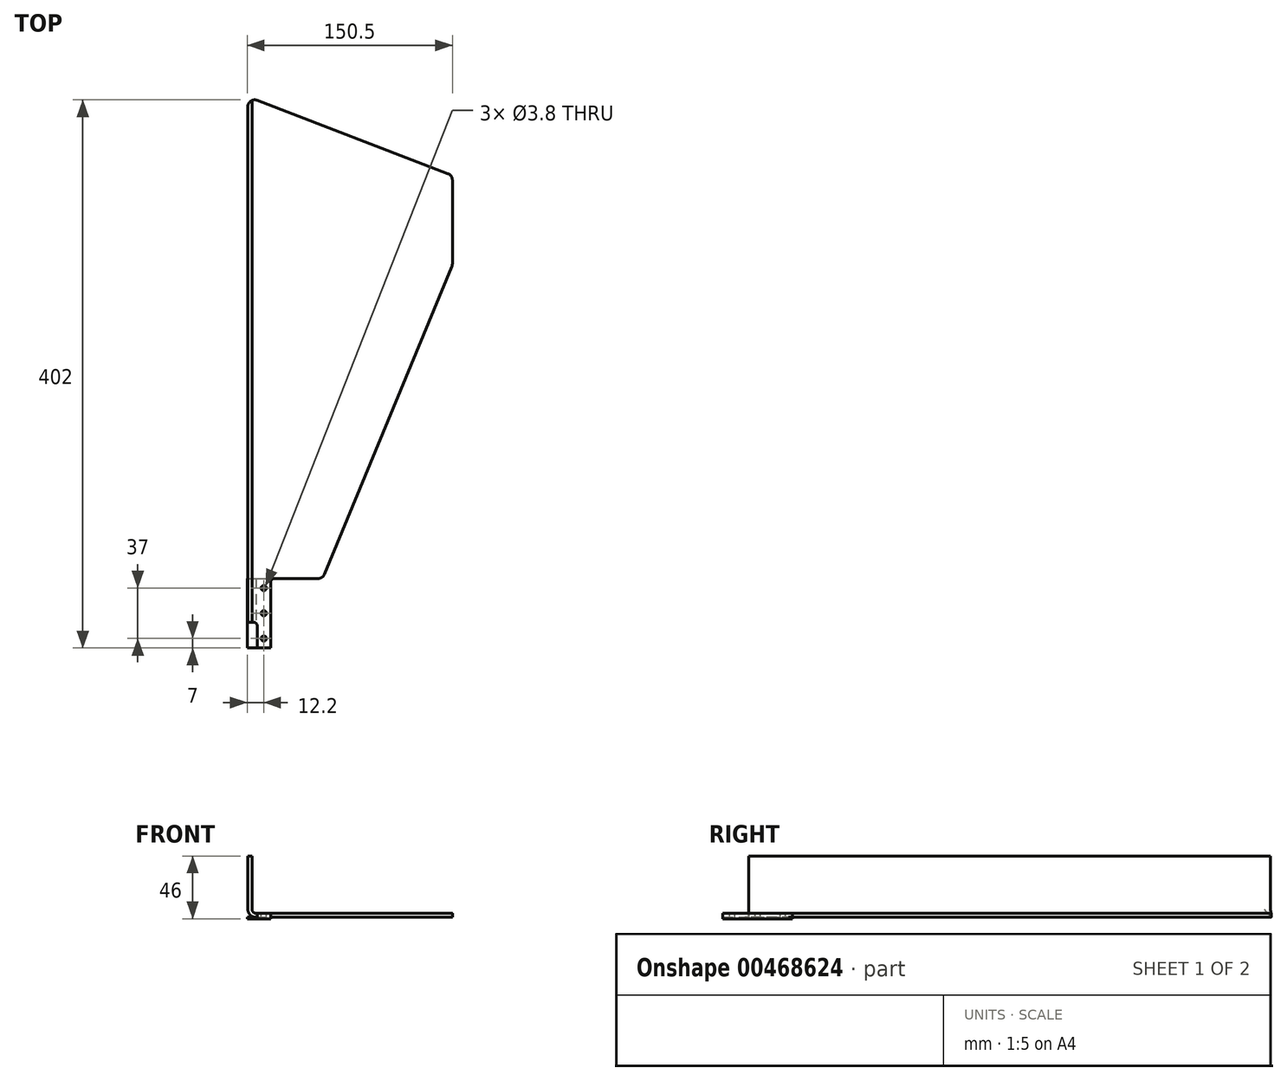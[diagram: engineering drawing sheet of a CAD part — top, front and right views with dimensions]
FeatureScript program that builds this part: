
annotation { "Feature Type Name" : "Feature", "Feature Type Description" : "" }
export const myFeature = defineFeature(function(context is Context, id is Id, definition is map)
    precondition{}
    {
        {
            var Q0;
            Q0=qCreatedBy(makeId("Front.planeOp"),FACE);
            var sketch = newSketch(context, id + "F0", { "sketchPlane" : qUnion([Q0]) });
            skLineSegment(sketch, "E0", {"start": v(-20, 42) * mm, "end": v(-20, 3) * mm});
            skLineSegment(sketch, "E1", {"start": v(-17, 0) * mm, "end": v(127, 0) * mm});
            skPoint(sketch, "E2", {"position": v(0, 0) * mm});
            skPoint(sketch, "E3.visualSharp", {"position": v(-20, 0) * mm});
            skArc(sketch, "E3.filletArc", {"start": v(-20, 3) * mm, "mid": v(-19.12, 0.88) * mm, "end": v(-17, 0) * mm});
            skLineSegment(sketch, "E4", {"start": v(-20, 42) * mm, "end": v(-23, 42) * mm});
            skLineSegment(sketch, "E5", {"start": v(-23, 42) * mm, "end": v(-23, 3) * mm});
            skLineSegment(sketch, "E6", {"start": v(-17, -3) * mm, "end": v(127, -3) * mm});
            skPoint(sketch, "E7.visualSharp", {"position": v(-23, -3) * mm});
            skArc(sketch, "E7.filletArc", {"start": v(-23, 3) * mm, "mid": v(-21.24, -1.24) * mm, "end": v(-17, -3) * mm});
            skLineSegment(sketch, "E8", {"start": v(127, 0) * mm, "end": v(127, -3) * mm});
            skSolve(sketch);
        }
        {
            var Q0;
            Q0=qSketchRegion(id+"F0",true);
            extrude(context, id + "F1", {"entities" : qUnion([Q0]), "oppositeDirection" : true, "depth" : 500 * mm});
        }
        {
            var Q0;
            Q0=qCreatedBy(makeId("Top.planeOp"),FACE);
            var sketch = newSketch(context, id + "F2", { "sketchPlane" : qUnion([Q0]) });
            skLineSegment(sketch, "E9.bottom", {"start": v(-56.37, 525.22) * mm, "end": v(165.37, 525.22) * mm});
            skLineSegment(sketch, "E9.top", {"start": v(-56.37, -13.1) * mm, "end": v(165.37, -13.1) * mm});
            skLineSegment(sketch, "E9.left", {"start": v(-56.37, 525.22) * mm, "end": v(-56.37, -13.1) * mm});
            skLineSegment(sketch, "E9.right", {"start": v(165.37, 525.22) * mm, "end": v(165.37, -13.1) * mm});
            skLineSegment(sketch, "E10.bottom", {"start": v(455.61, 344.43) * mm, "end": v(485.6, 345.09) * mm});
            skLineSegment(sketch, "E10.top", {"start": v(456.73, 293.44) * mm, "end": v(486.72, 294.1) * mm});
            skLineSegment(sketch, "E10.left", {"start": v(455.61, 344.43) * mm, "end": v(456.73, 293.44) * mm});
            skLineSegment(sketch, "E10.right", {"start": v(485.6, 345.09) * mm, "end": v(486.72, 294.1) * mm});
            skCircle(sketch, "E11", {"center": v(481.57, 300.99) * mm, "radius": 1.9 * mm});
            skCircle(sketch, "E12", {"center": v(480.76, 337.98) * mm, "radius": 1.9 * mm});
            skCircle(sketch, "E13", {"center": v(460.77, 337.54) * mm, "radius": 1.9 * mm});
            skCircle(sketch, "E14", {"center": v(461.57, 300.55) * mm, "radius": 1.9 * mm});
            skPoint(sketch, "E15", {"position": v(456.17, 318.94) * mm});
            skLineSegment(sketch, "E16.left", {"start": v(468.41, 344.71) * mm, "end": v(469.52, 293.72) * mm});
            skLineSegment(sketch, "E16.right", {"start": v(472.81, 344.8) * mm, "end": v(473.92, 293.82) * mm});
            skLineSegment(sketch, "E17.0", {"start": v(461.57, 300.55) * mm, "end": v(481.57, 300.99) * mm, "construction": true});
            skLineSegment(sketch, "E18.0", {"start": v(460.77, 337.54) * mm, "end": v(480.76, 337.98) * mm, "construction": true});
            skLineSegment(sketch, "E19.0", {"start": v(461.57, 300.55) * mm, "end": v(460.77, 337.54) * mm, "construction": true});
            skLineSegment(sketch, "E20.0", {"start": v(481.57, 300.99) * mm, "end": v(480.76, 337.98) * mm, "construction": true});
            skPoint(sketch, "E21", {"position": v(470.61, 344.76) * mm});
            skCircle(sketch, "E22", {"center": v(461.17, 319.05) * mm, "radius": 1.9 * mm});
            skCircle(sketch, "E23", {"center": v(481.16, 319.48) * mm, "radius": 1.9 * mm});
            skLineSegment(sketch, "E24", {"start": v(486.72, 294.1) * mm, "end": v(474.92, 293.84) * mm});
            skLineSegment(sketch, "E25", {"start": v(467.41, 344.69) * mm, "end": v(455.61, 344.43) * mm});
            skLineSegment(sketch, "E26.1.3", {"start": v(456.01, 326.28) * mm, "end": v(455.61, 344.43) * mm});
            skPoint(sketch, "E27", {"position": v(510.48, 432.74) * mm});
            skPoint(sketch, "E28.visualSharp", {"position": v(485.6, 345.09) * mm});
            skLineSegment(sketch, "E29", {"start": v(33.19, 54.09) * mm, "end": v(126.62, 279.65) * mm});
            skLineSegment(sketch, "E30", {"start": v(-23, 19) * mm, "end": v(-23, 397) * mm});
            skLineSegment(sketch, "E31", {"start": v(-16.2, 401.67) * mm, "end": v(123.8, 347.93) * mm});
            skLineSegment(sketch, "E32", {"start": v(-6.3, 0) * mm, "end": v(-6.3, 48) * mm});
            skLineSegment(sketch, "E33", {"start": v(-3.3, 51) * mm, "end": v(28.57, 51) * mm});
            skLineSegment(sketch, "E34", {"start": v(-23, 19) * mm, "end": v(-19, 19) * mm});
            skLineSegment(sketch, "E35", {"start": v(-16, 16) * mm, "end": v(-16, 0) * mm});
            skLineSegment(sketch, "E36", {"start": v(-16, 0) * mm, "end": v(-6.3, 0) * mm});
            skLineSegment(sketch, "E37", {"start": v(127, 343.26) * mm, "end": v(127, 281.57) * mm});
            skPoint(sketch, "E38.visualSharp", {"position": v(-23, 404.28) * mm});
            skArc(sketch, "E38.filletArc", {"start": v(-16.2, 401.67) * mm, "mid": v(-20.83, 401.12) * mm, "end": v(-23, 397) * mm});
            skPoint(sketch, "E39.visualSharp", {"position": v(127, 346.7) * mm});
            skArc(sketch, "E39.filletArc", {"start": v(127, 343.26) * mm, "mid": v(126.12, 346.1) * mm, "end": v(123.8, 347.93) * mm});
            skPoint(sketch, "E40.visualSharp", {"position": v(127, 280.57) * mm});
            skArc(sketch, "E40.filletArc", {"start": v(126.62, 279.65) * mm, "mid": v(126.9, 280.6) * mm, "end": v(127, 281.57) * mm});
            skPoint(sketch, "E41.visualSharp", {"position": v(31.9, 51) * mm});
            skArc(sketch, "E41.filletArc", {"start": v(28.57, 51) * mm, "mid": v(31.35, 51.84) * mm, "end": v(33.19, 54.09) * mm});
            skPoint(sketch, "E42.visualSharp", {"position": v(-16, 19) * mm});
            skArc(sketch, "E42.filletArc", {"start": v(-16, 16) * mm, "mid": v(-16.88, 18.12) * mm, "end": v(-19, 19) * mm});
            skArc(sketch, "E43.filletArc", {"start": v(-3.3, 51) * mm, "mid": v(-5.42, 50.12) * mm, "end": v(-6.3, 48) * mm});
            skCircle(sketch, "E44", {"center": v(-11.3, 7) * mm, "radius": 1.9 * mm});
            skCircle(sketch, "E45", {"center": v(-11.3, 44) * mm, "radius": 1.9 * mm});
            skLineSegment(sketch, "E46.0", {"start": v(-11.3, 7) * mm, "end": v(-11.3, 44) * mm, "construction": true});
            skCircle(sketch, "E47", {"center": v(-11.3, 25.5) * mm, "radius": 1.9 * mm});
            skSolve(sketch);
        }
        {
            var Q0;
            Q0=qSketchRegion(id+"F2",true);
            var Q1;
            Q1=makeQuery(id+"F2.imprint","IMPRINT",FACE,{"disambiguationData":[TD([[makeQuery(id+"F2.imprint","IMPRINT",EDGE,{"derivedFrom":sQuery(id+"F2.wireOp",EDGE,"E45")}),1.0]])]});
            var Q2;
            Q2=makeQuery(id+"F2.imprint","IMPRINT",FACE,{"disambiguationData":[TD([[makeQuery(id+"F2.imprint","IMPRINT",EDGE,{"derivedFrom":sQuery(id+"F2.wireOp",EDGE,"E47")}),1.0]])]});
            var Q3;
            Q3=makeQuery(id+"F2.imprint","IMPRINT",FACE,{"disambiguationData":[TD([[makeQuery(id+"F2.imprint","IMPRINT",EDGE,{"derivedFrom":sQuery(id+"F2.wireOp",EDGE,"E44")}),1.0]])]});
            extrude(context, id + "F3", {"entities" : qUnion([Q0, Q1, Q2, Q3]), "operationType" : NewBodyOperationType.REMOVE, "endBound" : BoundingType.SYMMETRIC, "oppositeDirection" : true, "depth" : 100 * mm});
        }
        {
            var Q0;
            Q0=makeQuery(id+"F1.opExtrude","SWEPT_FACE",FACE,{"disambiguationData":[OSD([sQuery(id+"F0.wireOp",EDGE,"E6")])]});
            var sketch = newSketch(context, id + "F4", { "sketchPlane" : qUnion([Q0]) });
            skLineSegment(sketch, "E48.bottom", {"start": v(-23.5, 0) * mm, "end": v(-6.3, 0) * mm});
            skLineSegment(sketch, "E48.top", {"start": v(-23.5, -51) * mm, "end": v(-6.3, -51) * mm});
            skLineSegment(sketch, "E48.right", {"start": v(-6.3, 0) * mm, "end": v(-6.3, -51) * mm});
            skCircle(sketch, "E49", {"center": v(-11.3, -44) * mm, "radius": 1.9 * mm});
            skCircle(sketch, "E50", {"center": v(-11.3, -7) * mm, "radius": 1.9 * mm});
            skLineSegment(sketch, "E51.left", {"start": v(-23.5, 0) * mm, "end": v(-23.5, -51) * mm});
            skLineSegment(sketch, "E51.right", {"start": v(-19.1, 0) * mm, "end": v(-19.1, -51) * mm});
            skLineSegment(sketch, "E52.0", {"start": v(-11.3, -44) * mm, "end": v(-11.3, -7) * mm, "construction": true});
            skCircle(sketch, "E53", {"center": v(-11.3, -25.5) * mm, "radius": 1.9 * mm});
            skPoint(sketch, "E54.visualSharp", {"position": v(-6.3, 0) * mm});
            skSolve(sketch);
        }
        {
            var Q0;
            Q0=qSketchRegion(id+"F4",true);
            extrude(context, id + "F5", {"entities" : qUnion([Q0]), "operationType" : NewBodyOperationType.ADD, "depth" : 1 * mm});
        }
    });
